# Revit family: 17.1  Канальный осевой вентилятор FE Тип B
name_source: partatom
category: Оборудование
revit_build: Autodesk Revit 2016 (Build: 20151209_0715(x64)
units: mm (PartAtom-declared; Revit-internal decimal feet)

## family parameters
Всегда вертикально = Да
На основе рабочей плоскости = Нет
Общий = Нет
При загрузке вырезать с полостями = Нет
Размер круглого соединителя = Использовать диаметр
Тип детали = Нормальный
Точка расчета площади = Нет

## types (5) — shared parameters
Е = 22 мм
Единица измерения = шт.
Завод изготовитель = KORF
И = 72 мм
Ключевая пометка = Вентиляция
Материал = Сталь серая
Мощность, кВт = 1 Вт
Наименование и тех.хар-ка = Канальный осевой вентилятор
Раздел = ОВ

## per-type parameters (varying)
| type | А | Б | Г | Г1 | Д | Д1 | Д2 | Д3 | Ж | Масса единицы | Размер В | Сила тока J, А | Тип, марка, обозначение | Частота вращения n, об/мин | х |
| FE045-4EF | 487 мм | 12 мм | 515 мм | 258 мм | 451 мм | 226 мм | 68 мм | 50 мм | 160 мм | 15.8 кг | 10 мм | 2.8 | FE045-4EF.4I.V7 | 1310 | 90 мм |
| FE050-VDF | 541 мм | 12 мм | 567 мм | 284 мм | 503 мм | 252 мм | 75 мм | 55 мм | 165 мм | 16.6 кг | 10 мм | 1.35 | FE050-VDF.4I.V7 | 1340 | 101 мм |
| FE050-4EF | 541 мм | 12 мм | 567 мм | 284 мм | 503 мм | 252 мм | 75 мм | 55 мм | 165 мм | 16.6 кг | 10 мм | 3.4 | FE050-4EF.4I.V7 | 1210 | 101 мм |
| FE056-VDF | 605 мм | 16 мм | 635 мм | 318 мм | 559 мм | 280 мм | 84 мм | 61 мм | 210 мм | 21 кг | 12 мм | 2.6 | FE056-VDF.4M.V7 | 1320 | 112 мм |
| FE063-6EF | 674 мм | 16 мм | 707 мм | 354 мм | 634 мм | 317 мм | 95 мм | 70 мм | 220 мм | 23 кг | 12 мм | 3.5 | FE063-6EF.4M.V7 | 900 | 127 мм |
